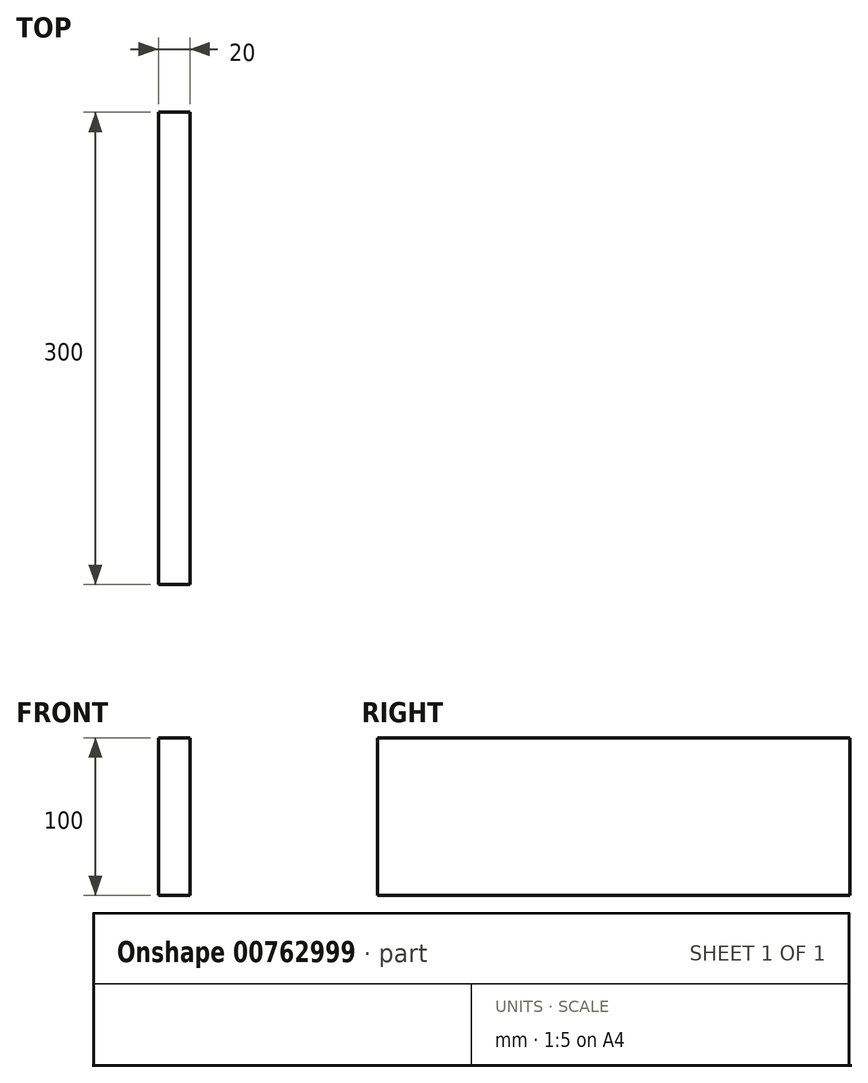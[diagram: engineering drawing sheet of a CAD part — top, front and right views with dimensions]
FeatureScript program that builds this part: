
annotation { "Feature Type Name" : "Feature", "Feature Type Description" : "" }
export const myFeature = defineFeature(function(context is Context, id is Id, definition is map)
    precondition{}
    {
        {
            var Q0;
            Q0=qCreatedBy(makeId("Front.planeOp"),FACE);
            var sketch = newSketch(context, id + "F0", { "sketchPlane" : qUnion([Q0])});
            skLineSegment(sketch, "E0.bottom", {"start": v(0, 0) * mm, "end": v(20, 0) * mm});
            skLineSegment(sketch, "E0.top", {"start": v(0, -100) * mm, "end": v(20, -100) * mm});
            skLineSegment(sketch, "E0.left", {"start": v(0, 0) * mm, "end": v(0, -100) * mm});
            skLineSegment(sketch, "E0.right", {"start": v(20, 0) * mm, "end": v(20, -100) * mm});
            skSolve(sketch);
        }
        {
            var Q0;
            Q0 = qSketchRegion(id + "F0", true);
            extrude(context, id + "F1", {"entities" : qUnion([Q0]), "depth" : 300 * mm, "offsetDistance" : 25 * mm});
        }
    });
